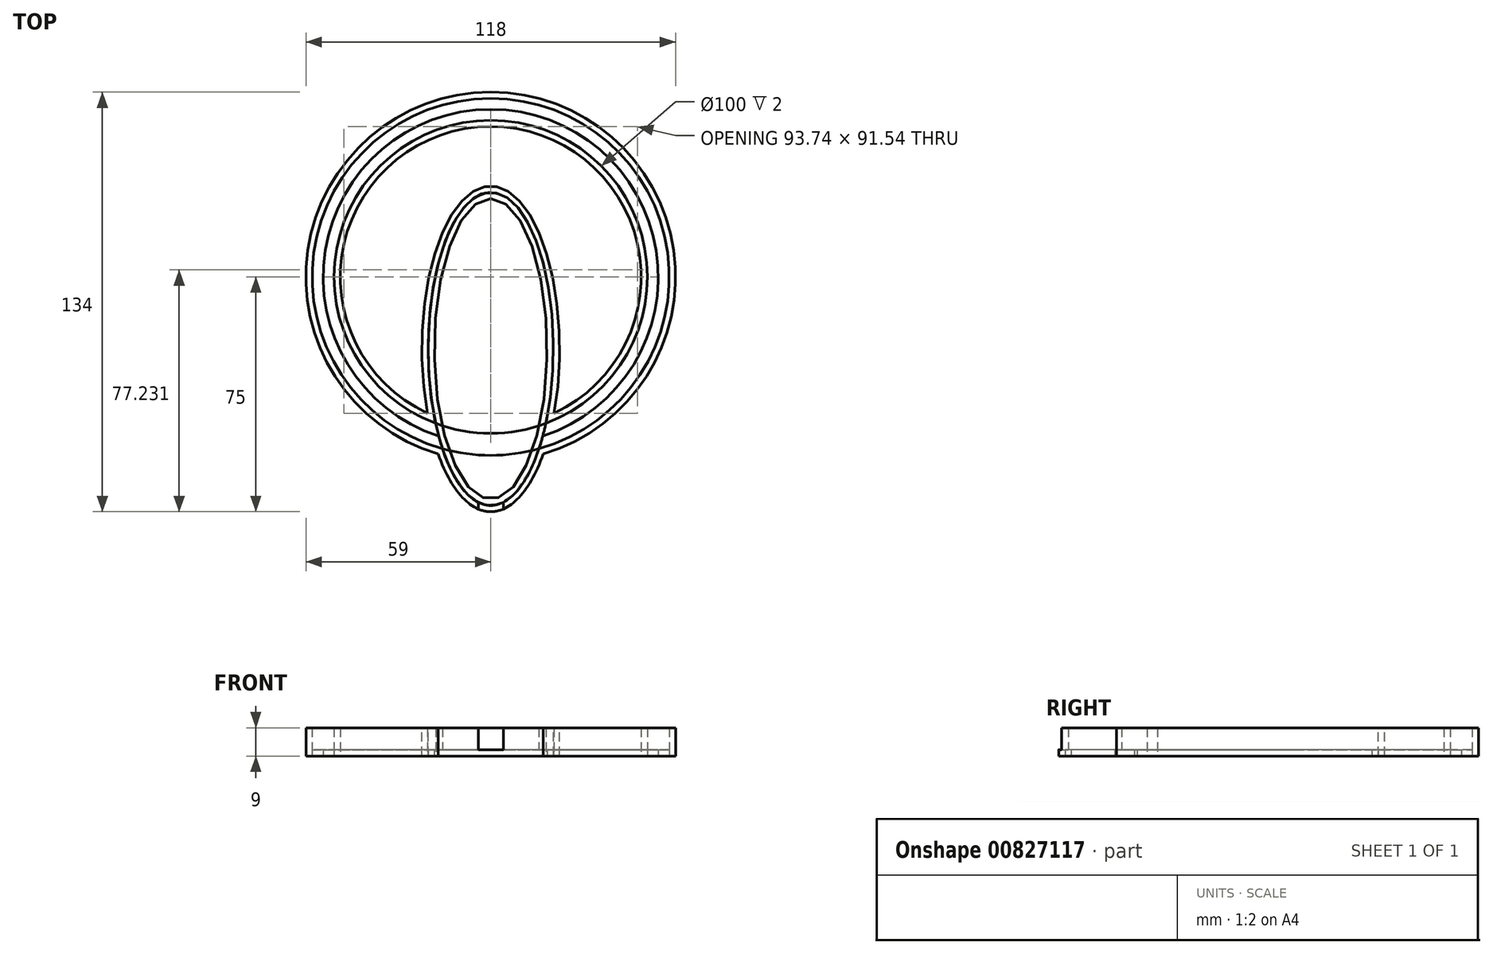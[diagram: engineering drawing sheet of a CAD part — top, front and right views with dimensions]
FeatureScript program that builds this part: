
annotation { "Feature Type Name" : "Feature", "Feature Type Description" : "" }
export const myFeature = defineFeature(function(context is Context, id is Id, definition is map)
    precondition{}
    {
        {
            var Q0;
            Q0=qCreatedBy(makeId("Top.planeOp"),FACE);
            var sketch = newSketch(context, id + "F0", { "sketchPlane" : qUnion([Q0])});
            skCircle(sketch, "E0", {"center": v(0, 0) * mm, "radius": 48 * mm});
            skCircle(sketch, "E1", {"center": v(0, 0) * mm, "radius": 50 * mm});
            skSolve(sketch);
        }
        {
            var Q0;
            Q0=makeQuery(id+"F0.imprint","IMPRINT",FACE,{"disambiguationData":[TD([[makeQuery(id+"F0.imprint","IMPRINT",EDGE,{"derivedFrom":sQuery(id+"F0.wireOp",EDGE,"E0")}),-1.0]])]});
            extrude(context, id + "F1", {"entities" : qUnion([Q0]), "depth" : 9 * mm, "offsetDistance" : 25 * mm});
        }
        {
            var Q0;
            Q0=qCreatedBy(makeId("Top.planeOp"),FACE);
            var sketch = newSketch(context, id + "F2", { "sketchPlane" : qUnion([Q0])});
            skCircle(sketch, "E2", {"center": v(0, 0) * mm, "radius": 50 * mm});
            skCircle(sketch, "E3", {"center": v(0, 0) * mm, "radius": 57 * mm});
            skSolve(sketch);
        }
        {
            var Q0;
            Q0=makeQuery(id+"F2.imprint","IMPRINT",FACE,{"disambiguationData":[TD([[makeQuery(id+"F2.imprint","IMPRINT",EDGE,{"derivedFrom":sQuery(id+"F2.wireOp",EDGE,"E2")}),-1.0]])]});
            extrude(context, id + "F3", {"entities" : qUnion([Q0]), "operationType" : NewBodyOperationType.ADD, "depth" : 2 * mm, "offsetDistance" : 25 * mm});
        }
        {
            var Q0;
            Q0=qCreatedBy(makeId("Top.planeOp"),FACE);
            var sketch = newSketch(context, id + "F4", { "sketchPlane" : qUnion([Q0])});
            skCircle(sketch, "E4", {"center": v(0, 0) * mm, "radius": 57 * mm});
            skCircle(sketch, "E5", {"center": v(0, 0) * mm, "radius": 59 * mm});
            skSolve(sketch);
        }
        {
            var Q0;
            Q0=makeQuery(id+"F4.imprint","IMPRINT",FACE,{"disambiguationData":[TD([[makeQuery(id+"F4.imprint","IMPRINT",EDGE,{"derivedFrom":sQuery(id+"F4.wireOp",EDGE,"E4")}),-1.0]])]});
            extrude(context, id + "F5", {"entities" : qUnion([Q0]), "operationType" : NewBodyOperationType.ADD, "depth" : 9 * mm, "offsetDistance" : 25 * mm});
        }
        {
            var Q0;
            Q0=qCreatedBy(makeId("Top.planeOp"),FACE);
            var sketch = newSketch(context, id + "F6", { "sketchPlane" : qUnion([Q0])});
            skEllipse(sketch, "E6", {"center": v(0, -23) * mm, "majorRadius": 52 * mm, "minorRadius": 22 * mm, "majorAxis": v(0, 1)});
            skEllipse(sketch, "E7", {"center": v(0, -23) * mm, "majorRadius": 50 * mm, "minorRadius": 20 * mm, "majorAxis": v(0, 1)});
            skSolve(sketch);
        }
        {
            var Q0;
            Q0=makeQuery(id+"F6.imprint","IMPRINT",FACE,{"disambiguationData":[TD([[makeQuery(id+"F6.imprint","IMPRINT",EDGE,{"derivedFrom":sQuery(id+"F6.wireOp",EDGE,"E6")}),1.0]])]});
            extrude(context, id + "F7", {"entities" : qUnion([Q0]), "operationType" : NewBodyOperationType.ADD, "depth" : 9 * mm, "offsetDistance" : 25 * mm});
        }
        {
            var Q0;
            Q0=qCreatedBy(makeId("Top.planeOp"),FACE);
            var sketch = newSketch(context, id + "F8", { "sketchPlane" : qUnion([Q0])});
            skEllipse(sketch, "E8", {"center": v(0, -23) * mm, "majorRadius": 50 * mm, "minorRadius": 20 * mm, "majorAxis": v(0, 1)});
            skSolve(sketch);
        }
        {
            var Q0;
            Q0=makeQuery(id+"F8.imprint","IMPRINT",FACE,{"disambiguationData":[TD([[makeQuery(id+"F8.imprint","IMPRINT",EDGE,{"derivedFrom":sQuery(id+"F8.wireOp",EDGE,"E8")}),1.0]])]});
            extrude(context, id + "F9", {"entities" : qUnion([Q0]), "operationType" : NewBodyOperationType.REMOVE, "depth" : 9 * mm, "offsetDistance" : 25 * mm});
        }
        {
            var Q0;
            Q0=qCreatedBy(makeId("Top.planeOp"),FACE);
            var sketch = newSketch(context, id + "F10", { "sketchPlane" : qUnion([Q0])});
            skCircle(sketch, "E9", {"center": v(0, 0) * mm, "radius": 50 * mm});
            skCircle(sketch, "E10", {"center": v(0, 0) * mm, "radius": 53.5 * mm});
            skSolve(sketch);
        }
        {
            var Q0;
            Q0=makeQuery(id+"F10.imprint","IMPRINT",FACE,{"disambiguationData":[TD([[makeQuery(id+"F10.imprint","IMPRINT",EDGE,{"derivedFrom":sQuery(id+"F10.wireOp",EDGE,"E9")}),-1.0]])]});
            extrude(context, id + "F11", {"entities" : qUnion([Q0]), "operationType" : NewBodyOperationType.REMOVE, "depth" : 9 * mm, "offsetDistance" : 25 * mm});
        }
        {
            var Q0;
            Q0=qCreatedBy(makeId("Top.planeOp"),FACE);
            var sketch = newSketch(context, id + "F12", { "sketchPlane" : qUnion([Q0])});
            skCircle(sketch, "E11", {"center": v(0, 0) * mm, "radius": 50 * mm});
            skCircle(sketch, "E12", {"center": v(0, 0) * mm, "radius": 57 * mm});
            skSolve(sketch);
        }
        {
            var Q0;
            Q0=makeQuery(id+"F12.imprint","IMPRINT",FACE,{"disambiguationData":[TD([[makeQuery(id+"F12.imprint","IMPRINT",EDGE,{"derivedFrom":sQuery(id+"F12.wireOp",EDGE,"E11")}),-1.0]])]});
            extrude(context, id + "F13", {"entities" : qUnion([Q0]), "depth" : 2 * mm, "offsetDistance" : 25 * mm});
        }
        {
            var Q0;
            Q0=qCreatedBy(makeId("Top.planeOp"),FACE);
            var sketch = newSketch(context, id + "F14", { "sketchPlane" : qUnion([Q0])});
            skEllipse(sketch, "E13", {"center": v(0, -23) * mm, "majorRadius": 48 * mm, "minorRadius": 18 * mm, "majorAxis": v(0, 1)});
            skSolve(sketch);
        }
        {
            var Q0;
            Q0=makeQuery(id+"F14.imprint","IMPRINT",FACE,{"disambiguationData":[TD([[makeQuery(id+"F14.imprint","IMPRINT",EDGE,{"derivedFrom":sQuery(id+"F14.wireOp",EDGE,"E13")}),1.0]])]});
            extrude(context, id + "F15", {"entities" : qUnion([Q0]), "depth" : 2 * mm, "offsetDistance" : 25 * mm});
        }
        {
            var Q0;
            Q0=makeQuery(id+"F15.opExtrude","CAP_FACE",FACE,{"disambiguationData":[OSD([sQuery(id+"F14.wireOp",EDGE,"E13")])],"isStart":false});
            cPlane(context, id + "F16", {"entities" : qUnion([Q0]), "cplaneType" : CPlaneType.OFFSET, "offset" : 0 * mm, "width" : 150 * mm, "height" : 150 * mm});
        }
        {
            var Q0;
            Q0=qCreatedBy(makeId("Front.planeOp"),FACE);
            var sketch = newSketch(context, id + "F17", { "sketchPlane" : qUnion([Q0])});
            skLineSegment(sketch, "E14.bottom", {"start": v(-4, 9) * mm, "end": v(4, 9) * mm});
            skLineSegment(sketch, "E14.top", {"start": v(-4, 2) * mm, "end": v(4, 2) * mm});
            skLineSegment(sketch, "E14.left", {"start": v(-4, 9) * mm, "end": v(-4, 2) * mm});
            skLineSegment(sketch, "E14.right", {"start": v(4, 9) * mm, "end": v(4, 2) * mm});
            skPoint(sketch, "E14.middle", {"position": v(0, 5.5) * mm});
            skSolve(sketch);
        }
        {
            var Q0;
            Q0=makeQuery(id+"F17.imprint","IMPRINT",FACE,{"disambiguationData":[TD([[makeQuery(id+"F17.imprint","IMPRINT",EDGE,{"derivedFrom":sQuery(id+"F17.wireOp",EDGE,"E14.bottom")}),-1.0]])]});
            extrude(context, id + "F18", {"entities" : qUnion([Q0]), "operationType" : NewBodyOperationType.REMOVE, "depth" : 80 * mm, "offsetDistance" : 25 * mm});
        }
        {
            var Q0;
            Q0=makeQuery(id+"F13.opExtrude","CAP_FACE",FACE,{"disambiguationData":[OSD([sQuery(id+"F12.wireOp",EDGE,"E11"),sQuery(id+"F12.wireOp",EDGE,"E12")])],"isStart":false});
            extrude(context, id + "F19", {"entities" : qUnion([Q0]), "operationType" : NewBodyOperationType.REMOVE, "depth" : 9 * mm, "offsetDistance" : 25 * mm});
        }
        {
            var Q0;
            Q0=qCreatedBy(makeId("Top.planeOp"),FACE);
            var sketch = newSketch(context, id + "F20", { "sketchPlane" : qUnion([Q0])});
            skEllipse(sketch, "E15", {"center": v(0, -23) * mm, "majorRadius": 50 * mm, "minorRadius": 20 * mm, "majorAxis": v(0, 1)});
            skSolve(sketch);
        }
        {
            var Q0;
            Q0=makeQuery(id+"F20.imprint","IMPRINT",FACE,{"disambiguationData":[TD([[makeQuery(id+"F20.imprint","IMPRINT",EDGE,{"derivedFrom":sQuery(id+"F20.wireOp",EDGE,"E15")}),1.0]])]});
            extrude(context, id + "F21", {"entities" : qUnion([Q0]), "depth" : 2 * mm, "offsetDistance" : 25 * mm});
        }
    });
